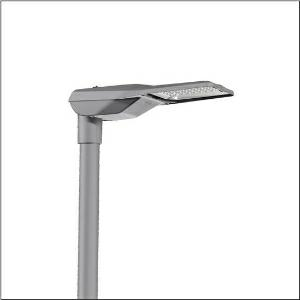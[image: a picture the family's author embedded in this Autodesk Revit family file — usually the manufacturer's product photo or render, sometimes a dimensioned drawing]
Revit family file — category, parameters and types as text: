
# Revit family: streetlight_sl_21_mini___p0_8a_5xe2u33s08gb_2c4a
name_source: partatom
category: Lighting Fixtures
units: mm (PartAtom-declared; Revit-internal decimal feet)

## family parameters
Cut with Voids When Loaded = No
Host = Face
Light Source = No
Part Type = Normal
Room Calculation Point = No
Round Connector Dimension = Use Diameter
Shared = No

## types (1)
- --- (1 x LED, 5990 lm, 40.4 W, 3000K)
    Apparent Load = 40 VA
    CIE Flux Codes = 33 69 96 100 100
    Color Rendering = 70
    Color Temperature = 3000K
    Default Elevation = 1800 mm
    Description = Streetlight SL 21 mini, mast luminaire, primary light control with lens, of PMMA, primary optical cover: cover, of toughened safety glass, transparent, light distribution: P0.8a, light emission: direct distribution, primary light characteristic: asymmetric, installation type: post-top, side-entry, LED, High Power LED, rated luminous flux: 5.990lm, luminous efficacy: 148lm/W, light colour: 730, colour temperature: 3000K, control gear: D4i, control: pre-setting: logarithmic dimming characteristic, flexible luminous flux parameterisation, time-dependent luminous flux control, constant luminous flux control, overheat protection, mains connection: 220..240V, AC, 50/60Hz, start of lifetime: 40W, end of service life: 41W, reduction: 19W, luminaire housing, of diecast aluminium, powder-coated, Siteco® metallic grey (DB 702S), corrosivity category C5 mid according to DIN EN ISO 12944, multi-level sealing system, sealing non-destructively replaceable, inclination adjustable: 0°, 5°, 10°, 15°, please order mast flange separately, length: 628mm, width: 235mm, height: 110mm, mast flange for spigot size: 42mm (side-entry): 5XC10008XM4, 60/48mm (side-entry/post-top): 5XC10108XM2, 76/60mm (side-entry/post-top): 5XC10108XM1, mounting height: 4..8m, Smart Interface above, protection rating (complete): IP66, insulation class (complete): insulation class II (safety insulation), certification: CE, ENEC, ENEC+, VDE, impact resistance: IK09, permissible operating ambient temperature for outdoor applications: -40..+50°C, standard-compliant lighting for roads and squares, packaging unit: 1 piece

Light Distribution: P0.8a
    Height = 110 mm
    Lamp = 1 x LED
    Lamp Light Flux = 5990 lm
    Lamp Power = 40.4 W
    Lamp count = 1
    Length = 625 mm
    Luminous efficacy = 148 lm/W
    Manufacturer = Siteco
    ModVariant = No
    Model = 5XE2U33S08GB
    Number of Poles = 1
    OnlyDefault = Yes
    Power Factor = 1
    Product Name = Streetlight SL 21 mini | P0.8a
    Product group = mast luminaire | pylon top
    ProductGroupID = 6100
    Protection Class = Protection class II
    Protection Degree = IP 66
    RLX_Detail_Level = 1
    RLX_Emergency_Light_Flux = 0 lm
    RLX_Emergency_Type = 0
    RLX_Emergency_Type_DB = No
    RlxData = <blob elided: 91609 chars, md5=1b43177a>
    Socket = socket
    Standby Power = 0 W
    System Light Flux = 5990 lm
    System Power = 40 W
    Type Comments = factory setting: luminous flux: 100 % | dim-lin: 254 | 812 mA
    Type Image = l_1003515.jpg
    URL = http://relux.com
    VarID = @adj_069218
    Voltage = 0 V
    Weight = 0.00 kg
    Width = 234 mm

## geometry (parser evidence)
native form markers: Blend x4, Sweep x12
no freeform markers — native parametric forms only
